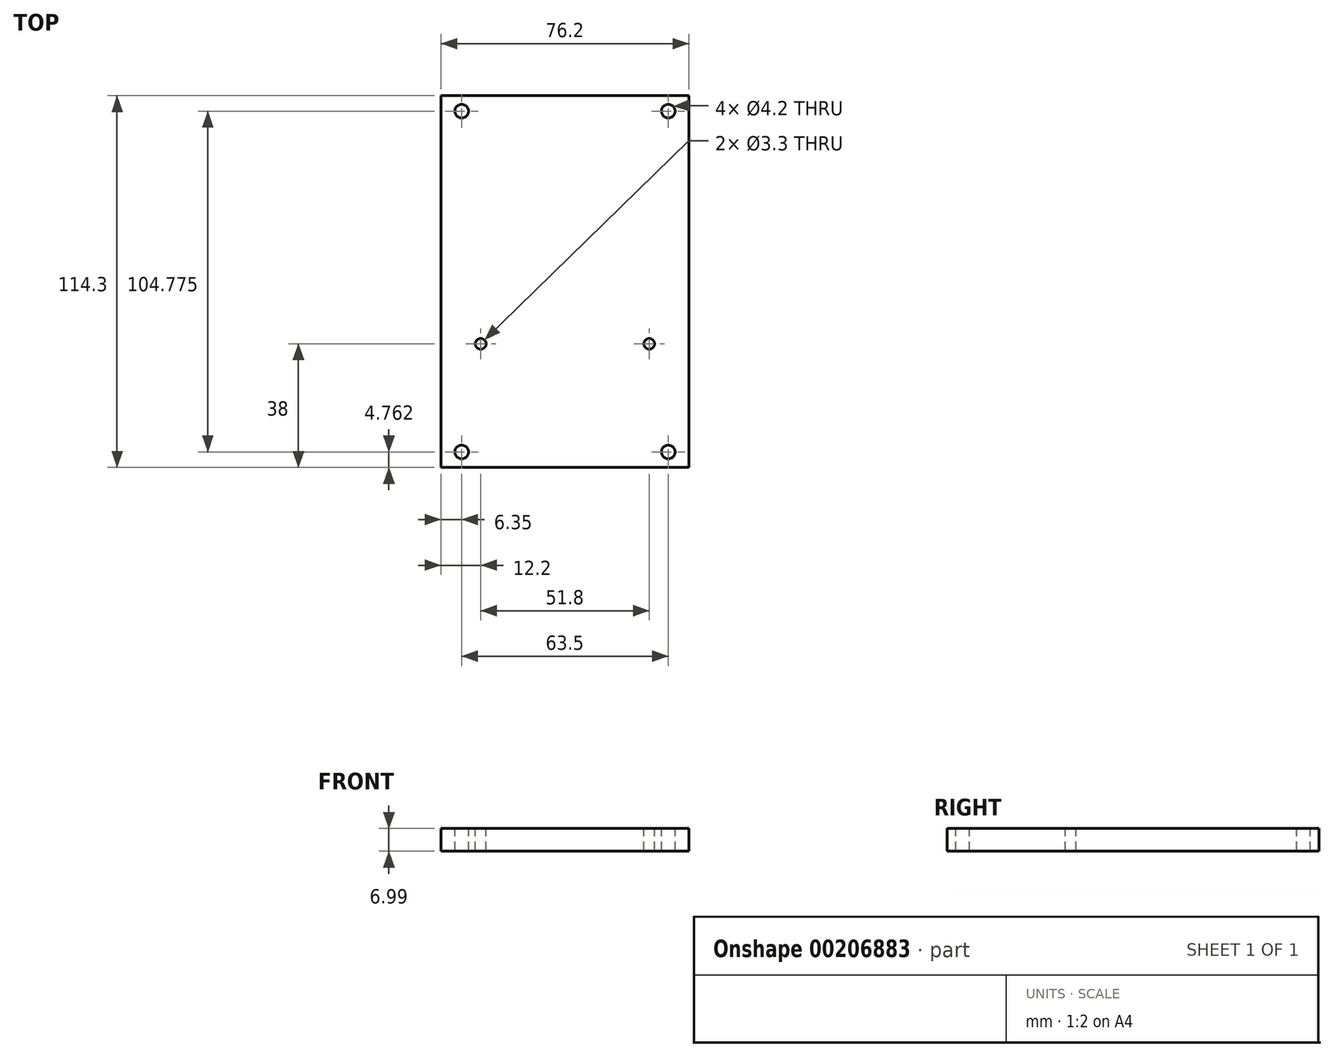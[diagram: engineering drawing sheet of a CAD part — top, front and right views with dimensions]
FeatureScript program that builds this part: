
annotation { "Feature Type Name" : "Feature", "Feature Type Description" : "" }
export const myFeature = defineFeature(function(context is Context, id is Id, definition is map)
    precondition{}
    {
        {
            var Q0;
            Q0=qCreatedBy(makeId("Top.planeOp"),FACE);
            var sketch = newSketch(context, id + "F0", { "sketchPlane" : qUnion([Q0])});
            skLineSegment(sketch, "E0.bottom", {"start": v(38.1, -57.15) * mm, "end": v(-38.1, -57.15) * mm});
            skLineSegment(sketch, "E0.top", {"start": v(38.1, 57.15) * mm, "end": v(-38.1, 57.15) * mm});
            skLineSegment(sketch, "E0.left", {"start": v(38.1, -57.15) * mm, "end": v(38.1, 57.15) * mm});
            skLineSegment(sketch, "E0.right", {"start": v(-38.1, -57.15) * mm, "end": v(-38.1, 57.15) * mm});
            skPoint(sketch, "E0.middle", {"position": v(0, 0) * mm});
            skSolve(sketch);
        }
        {
            var Q0;
            Q0=qSketchRegion(id+"F0",true);
            extrude(context, id + "F1", {"entities" : qUnion([Q0]), "depth" : 7 * mm});
        }
        {
            var Q0;
            Q0=makeQuery(id+"F1.opExtrude","CAP_FACE",FACE,{"disambiguationData":[OSD([sQuery(id+"F0.wireOp",EDGE,"E0.bottom"),sQuery(id+"F0.wireOp",EDGE,"E0.top"),sQuery(id+"F0.wireOp",EDGE,"E0.left"),sQuery(id+"F0.wireOp",EDGE,"E0.right")])],"isStart":false});
            var sketch = newSketch(context, id + "F2", { "sketchPlane" : qUnion([Q0])});
            skPoint(sketch, "E1", {"position": v(-31.75, 52.39) * mm});
            skPoint(sketch, "E2.0.1.0", {"position": v(-31.75, -52.39) * mm});
            skPoint(sketch, "E2.1.0.0", {"position": v(31.75, 52.39) * mm});
            skPoint(sketch, "E2.1.1.0", {"position": v(31.75, -52.39) * mm});
            skLineSegment(sketch, "E2.direction1", {"start": v(-31.75, 52.39) * mm, "end": v(31.75, 52.39) * mm, "construction": true});
            skLineSegment(sketch, "E2.direction2", {"start": v(-31.75, 52.39) * mm, "end": v(-31.75, -52.39) * mm, "construction": true});
            skSolve(sketch);
        }
        {
            var Q0;
            Q0=sQuery(id+"F2.wireOp",VERTEX,"E1");
            var Q1;
            Q1=sQuery(id+"F2.wireOp",VERTEX,"E2.1.0.0");
            var Q2;
            Q2=sQuery(id+"F2.wireOp",VERTEX,"E2.1.1.0");
            var Q3;
            Q3=sQuery(id+"F2.wireOp",VERTEX,"E2.0.1.0");
            var Q4;
            Q4=makeQuery(id+"F1.opExtrude","SWEPT_BODY",BODY,{"disambiguationData":[OSD([sQuery(id+"F0.wireOp",EDGE,"E0.bottom"),sQuery(id+"F0.wireOp",EDGE,"E0.top"),sQuery(id+"F0.wireOp",EDGE,"E0.left"),sQuery(id+"F0.wireOp",EDGE,"E0.right")])]});
            hole(context, id + "F3", {"style" : HoleStyle.SIMPLE, "endStyle" : HoleEndStyle.THROUGH, "standardTappedOrClearance" : lookupTablePath({ "standard" : "ISO", "fit" : "Close", "size" : "M4", "type" : "Clearance" }), "standardBlindInLast" : lookupTablePath({ "fit" : "Close", "standard" : "ISO", "size" : "M4", "type" : "Clearance" }), "holeDiameter" : 4.2 * mm, "startFromSketch" : true, "locations" : qUnion([Q0, Q1, Q2, Q3]), "scope" : qUnion([Q4]), "isTappedThrough" : true});
        }
        {
            var Q0;
            Q0=makeQuery(id+"F1.opExtrude","SWEPT_FACE",FACE,{"disambiguationData":[OSD([sQuery(id+"F0.wireOp",EDGE,"E0.bottom")])]});
            var sketch = newSketch(context, id + "F4", { "sketchPlane" : qUnion([Q0])});
            skCircle(sketch, "E3", {"center": v(0, 4.03) * mm, "radius": 1.27 * mm});
            skSolve(sketch);
        }
        {
            var Q0;
            Q0=makeQuery(id+"F1.opExtrude","CAP_FACE",FACE,{"disambiguationData":[OSD([sQuery(id+"F0.wireOp",EDGE,"E0.bottom"),sQuery(id+"F0.wireOp",EDGE,"E0.top"),sQuery(id+"F0.wireOp",EDGE,"E0.left"),sQuery(id+"F0.wireOp",EDGE,"E0.right")])],"isStart":false});
            var sketch = newSketch(context, id + "F5", { "sketchPlane" : qUnion([Q0])});
            skPoint(sketch, "E4", {"position": v(-25.9, -19.15) * mm});
            skPoint(sketch, "E5", {"position": v(25.9, -19.15) * mm});
            skSolve(sketch);
        }
        {
            var Q0;
            Q0=sQuery(id+"F5.wireOp",VERTEX,"E4");
            var Q1;
            Q1=sQuery(id+"F5.wireOp",VERTEX,"E5");
            var Q2;
            Q2=sQuery(id+"FI7jx1AOZCxDqrO_1.1.F5.wireOp",VERTEX,"E5");
            var Q3;
            Q3=sQuery(id+"FI7jx1AOZCxDqrO_1.1.F5.wireOp",VERTEX,"E4");
            var Q4;
            Q4=makeQuery(id+"F1.opExtrude","SWEPT_BODY",BODY,{"disambiguationData":[OSD([sQuery(id+"F0.wireOp",EDGE,"E0.bottom"),sQuery(id+"F0.wireOp",EDGE,"E0.top"),sQuery(id+"F0.wireOp",EDGE,"E0.left"),sQuery(id+"F0.wireOp",EDGE,"E0.right")])]});
            hole(context, id + "F6", {"style" : HoleStyle.SIMPLE, "endStyle" : HoleEndStyle.BLIND, "standardTappedOrClearance" : lookupTablePath({ "standard" : "ISO", "engagement" : "75%", "pitch" : "0.7 mm", "size" : "M4", "type" : "Tapped" }), "standardBlindInLast" : lookupTablePath({ "standard" : "ISO", "engagement" : "75%", "pitch" : "0.7 mm", "size" : "M4", "type" : "Tapped" }), "holeDiameter" : 3.3 * mm, "holeDepth" : 12 * mm, "startFromSketch" : true, "locations" : qUnion([Q0, Q1, Q2, Q3]), "scope" : qUnion([Q4]), "majorDiameter" : 4 * mm});
        }
    });
